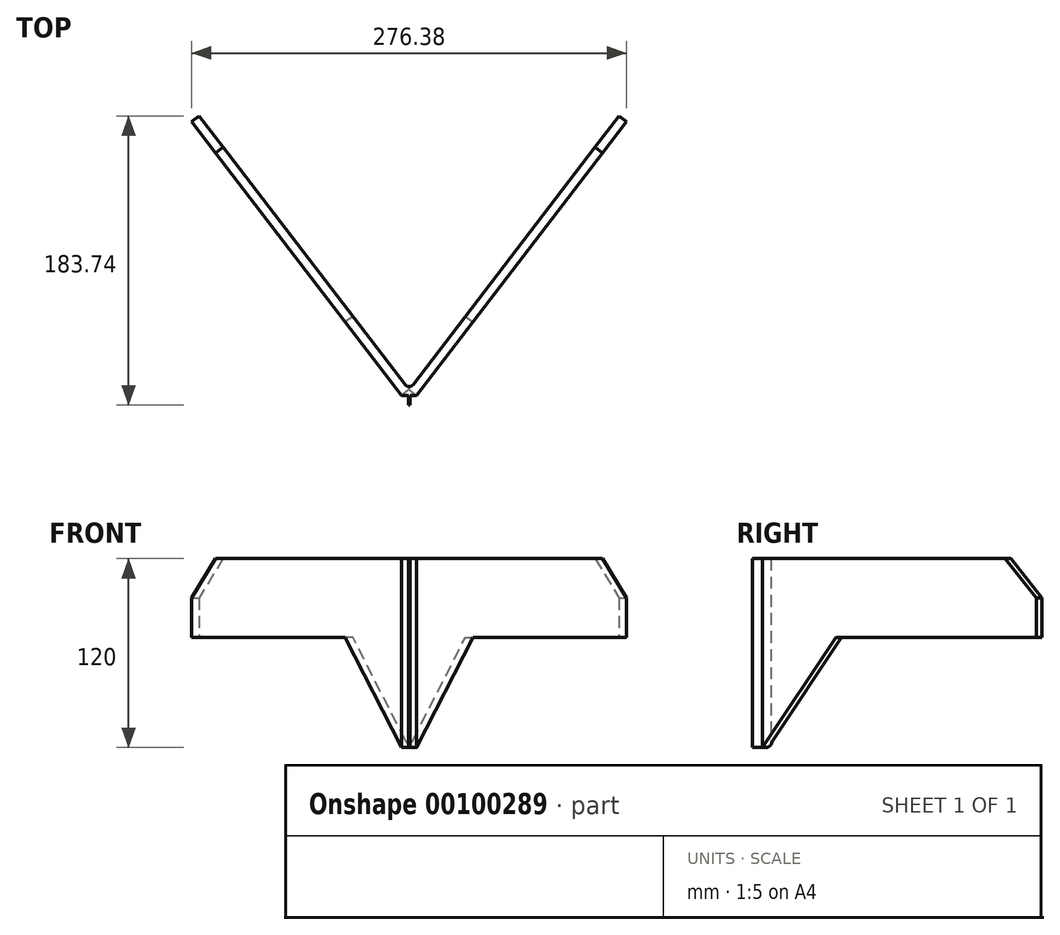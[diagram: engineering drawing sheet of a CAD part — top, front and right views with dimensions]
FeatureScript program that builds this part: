
annotation { "Feature Type Name" : "Feature", "Feature Type Description" : "" }
export const myFeature = defineFeature(function(context is Context, id is Id, definition is map)
    precondition{}
    {
        {
            var Q0;
            Q0=qCreatedBy(makeId("Top.planeOp"),FACE);
            var sketch = newSketch(context, id + "F0", { "sketchPlane" : qUnion([Q0])});
            skLineSegment(sketch, "E0", {"start": v(-138.19, 180.1) * mm, "end": v(-4.76, 6.2) * mm});
            skLineSegment(sketch, "E1", {"start": v(4.76, 6.2) * mm, "end": v(138.19, 180.1) * mm});
            skPoint(sketch, "E2.visualSharp", {"position": v(0, 0) * mm});
            skArc(sketch, "E2.filletArc", {"start": v(-4.76, 6.2) * mm, "mid": v(0, 3.86) * mm, "end": v(4.76, 6.2) * mm});
            skLineSegment(sketch, "E3", {"start": v(-138.19, 180.1) * mm, "end": v(-133.43, 183.74) * mm});
            skLineSegment(sketch, "E4", {"start": v(-133.43, 183.74) * mm, "end": v(-2.38, 12.96) * mm});
            skLineSegment(sketch, "E5", {"start": v(138.19, 180.1) * mm, "end": v(133.43, 183.74) * mm});
            skLineSegment(sketch, "E6", {"start": v(133.43, 183.74) * mm, "end": v(2.38, 12.96) * mm});
            skArc(sketch, "E7.filletArc", {"start": v(-2.38, 12.96) * mm, "mid": v(0, 11.78) * mm, "end": v(2.38, 12.96) * mm});
            skSolve(sketch);
        }
        {
            var Q0;
            Q0 = qSketchRegion(id + "F0", true);
            extrude(context, id + "F1", {"entities" : qUnion([Q0]), "depth" : 50 * mm, "hasSecondDirection" : true, "secondDirectionOppositeDirection" : true, "secondDirectionDepth" : 70 * mm});
        }
        {
            var Q0;
            Q0=makeQuery(id+"F1.opExtrude","CAP_EDGE",EDGE,{"disambiguationData":[OSD([sQuery(id+"F0.wireOp",EDGE,"E3")])],"isStart":false});
            var Q1;
            Q1=makeQuery(id+"F1.opExtrude","CAP_EDGE",EDGE,{"disambiguationData":[OSD([sQuery(id+"F0.wireOp",EDGE,"E5")])],"isStart":false});
            chamfer(context, id + "F2", {"entities" : qUnion([Q0, Q1]), "width" : 25 * mm, "tangentPropagation" : true});
        }
        {
            var Q0;
            Q0=makeQuery(id+"F1.opExtrude","SWEPT_FACE",FACE,{"disambiguationData":[OSD([sQuery(id+"F0.wireOp",EDGE,"E0")])]});
            var sketch = newSketch(context, id + "F3", { "sketchPlane" : qUnion([Q0])});
            skLineSegment(sketch, "E8", {"start": v(-227, 0) * mm, "end": v(-66.56, 0) * mm});
            skLineSegment(sketch, "E9", {"start": v(-66.56, 0) * mm, "end": v(-7.82, -70) * mm});
            skLineSegment(sketch, "E10.0", {"start": v(-227, -70) * mm, "end": v(-7.82, -70) * mm});
            skLineSegment(sketch, "E11.0", {"start": v(-227, 0) * mm, "end": v(-227, -70) * mm});
            skSolve(sketch);
        }
        {
            var Q0;
            Q0 = qSketchRegion(id + "F3", true);
            extrude(context, id + "F4", {"entities" : qUnion([Q0]), "operationType" : NewBodyOperationType.REMOVE, "oppositeDirection" : true, "depth" : 25 * mm});
        }
        {
            var Q0;
            Q0=makeQuery(id+"F1.opExtrude","SWEPT_FACE",FACE,{"disambiguationData":[OSD([sQuery(id+"F0.wireOp",EDGE,"E1")])]});
            var sketch = newSketch(context, id + "F5", { "sketchPlane" : qUnion([Q0])});
            skLineSegment(sketch, "E12", {"start": v(7.82, -70) * mm, "end": v(66.56, 0) * mm});
            skLineSegment(sketch, "E13", {"start": v(66.56, 0) * mm, "end": v(227, 0) * mm});
            skLineSegment(sketch, "E14.0", {"start": v(7.82, -70) * mm, "end": v(227, -70) * mm});
            skLineSegment(sketch, "E15.0", {"start": v(227, 0) * mm, "end": v(227, -70) * mm});
            skPoint(sketch, "E16.orphan", {"position": v(227, 25) * mm});
            skSolve(sketch);
        }
        {
            var Q0;
            Q0 = qSketchRegion(id + "F5", true);
            extrude(context, id + "F6", {"entities" : qUnion([Q0]), "operationType" : NewBodyOperationType.REMOVE, "oppositeDirection" : true, "depth" : 25 * mm});
        }
        {
            var Q0;
            Q0=qCreatedBy(makeId("Top.planeOp"),FACE);
            var sketch = newSketch(context, id + "F7", { "sketchPlane" : qUnion([Q0])});
            skLineSegment(sketch, "E17.top", {"start": v(-4.76, 0) * mm, "end": v(4.74, 0) * mm});
            skLineSegment(sketch, "E17.left", {"start": v(-4.76, 6.2) * mm, "end": v(-4.76, 0) * mm});
            skLineSegment(sketch, "E17.right", {"start": v(4.74, 6.2) * mm, "end": v(4.74, 0) * mm});
            skLineSegment(sketch, "E18", {"start": v(-4.76, 6.2) * mm, "end": v(4.76, 6.2) * mm});
            skSolve(sketch);
        }
        {
            var Q0;
            Q0=makeQuery(id+"F7.imprint","IMPRINT",FACE,{"disambiguationData":[TD([[makeQuery(id+"F7.imprint","IMPRINT",EDGE,{"derivedFrom":sQuery(id+"F7.wireOp",EDGE,"E17.top")}),1.0]])]});
            extrude(context, id + "F8", {"entities" : qUnion([Q0]), "operationType" : NewBodyOperationType.REMOVE, "depth" : 150 * mm, "hasSecondDirection" : true, "secondDirectionOppositeDirection" : true, "secondDirectionDepth" : 150 * mm});
        }
        {
            var Q0;
            Q0=qCreatedBy(makeId("Right.planeOp"),FACE);
            var sketch = newSketch(context, id + "F9", { "sketchPlane" : qUnion([Q0])});
            skLineSegment(sketch, "E19.bottom", {"start": v(6.2, 50) * mm, "end": v(0, 50) * mm});
            skLineSegment(sketch, "E19.top", {"start": v(6.2, -70) * mm, "end": v(0, -70) * mm});
            skLineSegment(sketch, "E19.left", {"start": v(6.2, 50) * mm, "end": v(6.2, -70) * mm});
            skLineSegment(sketch, "E19.right", {"start": v(0, 50) * mm, "end": v(0, -70) * mm});
            skSolve(sketch);
        }
        {
            var Q0;
            Q0 = qSketchRegion(id + "F9", true);
            extrude(context, id + "F10", {"entities" : qUnion([Q0]), "operationType" : NewBodyOperationType.ADD, "endBound" : BoundingType.SYMMETRIC, "depth" : 1 * mm});
        }
    });
